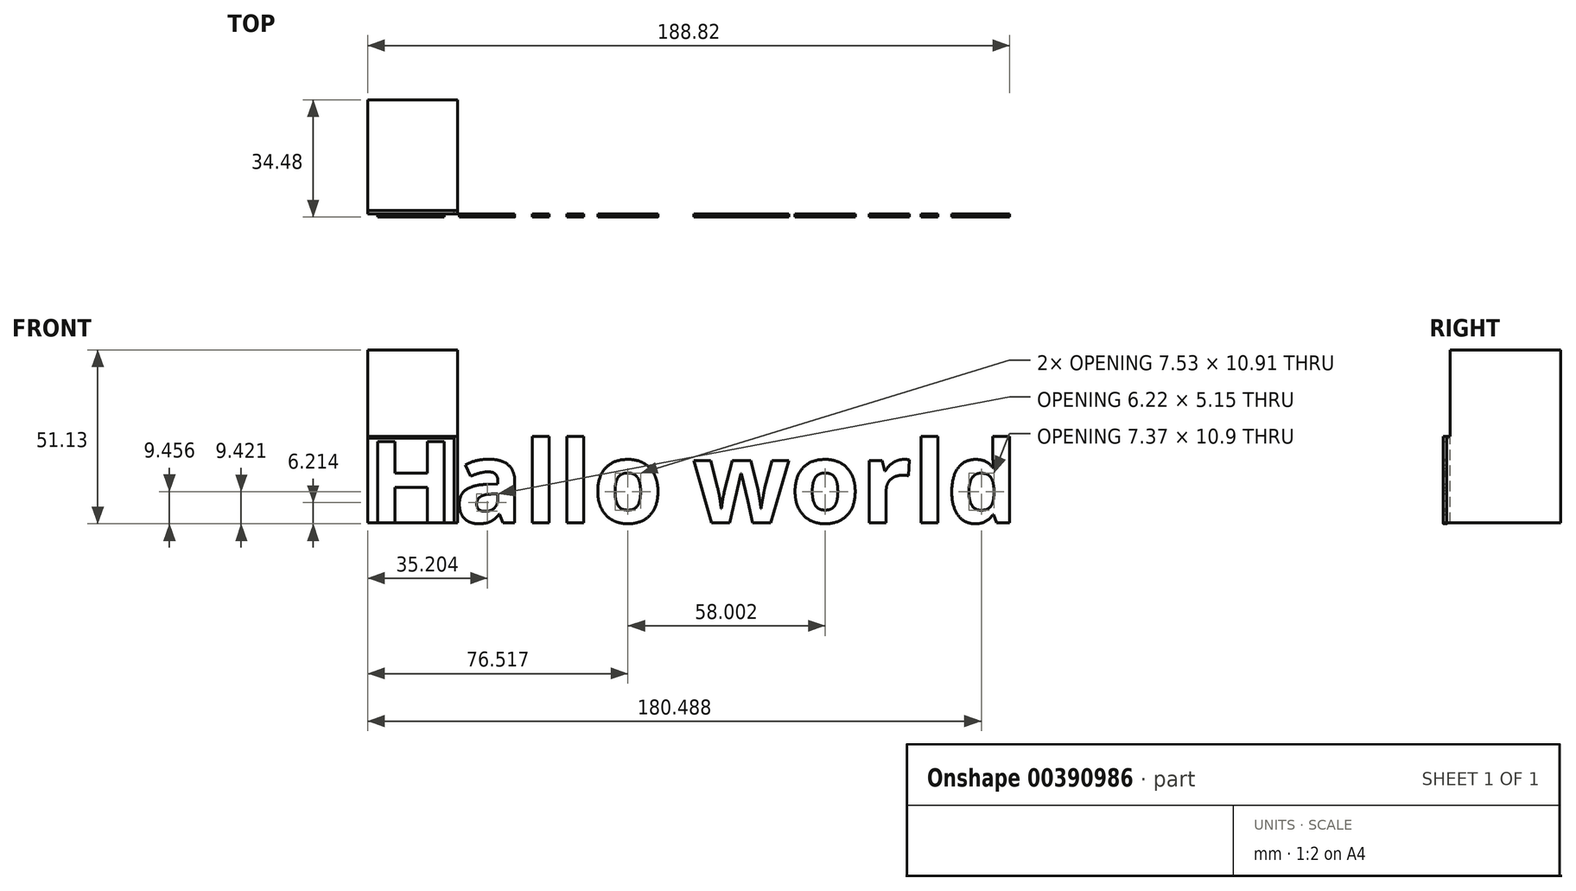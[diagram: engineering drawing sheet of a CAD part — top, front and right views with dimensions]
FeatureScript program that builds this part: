
annotation { "Feature Type Name" : "Feature", "Feature Type Description" : "" }
export const myFeature = defineFeature(function(context is Context, id is Id, definition is map)
    precondition{}
    {
        {
            var Q0;
            Q0=qCreatedBy(makeId("Top.planeOp"),FACE);
            var sketch = newSketch(context, id + "F0", { "sketchPlane" : qUnion([Q0])});
            skLineSegment(sketch, "E0.bottom", {"start": v(0, 0) * mm, "end": v(26.44, 0) * mm});
            skLineSegment(sketch, "E0.top", {"start": v(0, 32.48) * mm, "end": v(26.44, 32.48) * mm});
            skLineSegment(sketch, "E0.left", {"start": v(0, 0) * mm, "end": v(0, 32.48) * mm});
            skLineSegment(sketch, "E0.right", {"start": v(26.44, 0) * mm, "end": v(26.44, 32.48) * mm});
            skSolve(sketch);
        }
        {
            var Q0;
            Q0=makeQuery(id+"F0.imprint","IMPRINT",FACE,{"disambiguationData":[TD([[makeQuery(id+"F0.imprint","IMPRINT",EDGE,{"derivedFrom":sQuery(id+"F0.wireOp",EDGE,"E0.bottom")}),1.0]])]});
            extrude(context, id + "F1", {"entities" : qUnion([Q0]), "depth" : 25.4 * mm});
        }
        {
            var Q0;
            Q0=makeQuery(id+"F1.opExtrude","SWEPT_FACE",FACE,{"disambiguationData":[OSD([sQuery(id+"F0.wireOp",EDGE,"E0.bottom")])]});
            var sketch = newSketch(context, id + "F2", { "sketchPlane" : qUnion([Q0])});
            skSolve(sketch);
        }
        {
            var Q0;
            Q0 = qSketchRegion(id + "F2", true);
            var Q1;
            {var subQ0=sQuery(id+"F0.wireOp",EDGE,"E0.bottom");Q1=makeQuery(id+"F2.imprint","IMPRINT",FACE,{"disambiguationData":[TD([[makeQuery(id+"F2.imprint","IMPRINT",EDGE,{"derivedFrom":makeQuery(id+"F1.opExtrude","CAP_EDGE",EDGE,{"disambiguationData":[OSD([subQ0])],"isStart":true})}),1.0]])]});}
            var Q2;
            Q2 = qSketchRegion(id + "Fvldm2TemygVzHW_1", true);
            extrude(context, id + "F3", {"entities" : qUnion([Q0, Q1, Q2]), "depth" : 1 * mm});
        }
        {
            var Q0;
            Q0=makeQuery(id+"F3.opExtrude","CAP_FACE",FACE,{"disambiguationData":[OSD([sQuery(id+"F0.wireOp",EDGE,"E0.bottom"),sQuery(id+"F0.wireOp",EDGE,"E0.left"),sQuery(id+"F0.wireOp",EDGE,"E0.right")])],"isStart":false});
            var sketch = newSketch(context, id + "F4", { "sketchPlane" : qUnion([Q0])});
            skSolve(sketch);
        }
        {
            var Q0;
            {var subQ0=sQuery(id+"F0.wireOp",EDGE,"E0.bottom");Q0=makeQuery(id+"F4.imprint","IMPRINT",FACE,{"disambiguationData":[TD([[makeQuery(id+"F4.imprint","IMPRINT",EDGE,{"derivedFrom":makeQuery(id+"F3.opExtrude","CAP_EDGE",EDGE,{"disambiguationData":[OSD([subQ0]),TDD([makeQuery(id+"F2.imprint","IMPRINT",EDGE,{"derivedFrom":makeQuery(id+"F1.opExtrude","CAP_EDGE",EDGE,{"disambiguationData":[OSD([subQ0])],"isStart":true})})])],"isStart":false})}),1.0]])]});}
            var sketch = newSketch(context, id + "F5", { "sketchPlane" : qUnion([Q0])});
            skText(sketch, "E1", { "text": "Hallo world", "fontName": "OpenSans-Bold.ttf"});
            const initialGuessF5  = {"E1": [0, 0, 1, 0, 0.02407]};
            skSetInitialGuess(sketch, initialGuessF5);
            skSolve(sketch);
        }
        {
            var Q0;
            Q0=qCreatedBy(makeId("Front.planeOp"),FACE);
            var sketch = newSketch(context, id + "F6", { "sketchPlane" : qUnion([Q0])});
            skLineSegment(sketch, "E2.bottom", {"start": v(0, 0) * mm, "end": v(25.48, 0) * mm});
            skLineSegment(sketch, "E2.top", {"start": v(0, 24.84) * mm, "end": v(25.48, 24.84) * mm});
            skLineSegment(sketch, "E2.left", {"start": v(0, 0) * mm, "end": v(0, 24.84) * mm});
            skLineSegment(sketch, "E2.right", {"start": v(25.48, 0) * mm, "end": v(25.48, 24.84) * mm});
            skSolve(sketch);
        }
        {
            var Q0;
            Q0 = qSketchRegion(id + "F6", true);
            var Q1;
            Q1 = qSketchRegion(id + "F5", true);
            extrude(context, id + "F7", {"entities" : qUnion([Q0, Q1]), "depth" : 1 * mm});
        }
        {
            var Q0;
            Q0=makeQuery(id+"F1.opExtrude","CAP_FACE",FACE,{"disambiguationData":[OSD([sQuery(id+"F0.wireOp",EDGE,"E0.bottom"),sQuery(id+"F0.wireOp",EDGE,"E0.top"),sQuery(id+"F0.wireOp",EDGE,"E0.left"),sQuery(id+"F0.wireOp",EDGE,"E0.right")])],"isStart":false});
            var sketch = newSketch(context, id + "F8", { "sketchPlane" : qUnion([Q0])});
            skSolve(sketch);
        }
        {
            var Q0;
            Q0=makeQuery(id+"F1.opExtrude","CAP_FACE",FACE,{"disambiguationData":[OSD([sQuery(id+"F0.wireOp",EDGE,"E0.bottom"),sQuery(id+"F0.wireOp",EDGE,"E0.top"),sQuery(id+"F0.wireOp",EDGE,"E0.left"),sQuery(id+"F0.wireOp",EDGE,"E0.right")])],"isStart":false});
            var Q1;
            Q1=makeQuery(id+"F8.imprint","IMPRINT",FACE,{"disambiguationData":[TD([[makeQuery(id+"F8.imprint","IMPRINT",EDGE,{"derivedFrom":makeQuery(id+"F1.opExtrude","CAP_EDGE",EDGE,{"disambiguationData":[OSD([sQuery(id+"F0.wireOp",EDGE,"E0.bottom")])],"isStart":false})}),1.0]])]});
            extrude(context, id + "F9", {"entities" : qUnion([Q0, Q1]), "operationType" : NewBodyOperationType.ADD, "depth" : 25.4 * mm});
        }
    });
